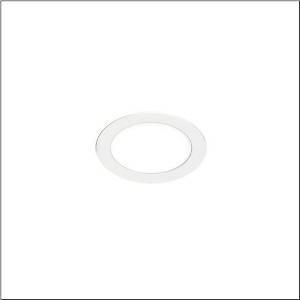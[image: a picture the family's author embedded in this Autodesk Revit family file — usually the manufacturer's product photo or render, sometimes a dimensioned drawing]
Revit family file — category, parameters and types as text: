
# Revit family: lunis_41_flat_51dr107dhba
name_source: partatom
category: Lighting Fixtures
units: mm (PartAtom-declared; Revit-internal decimal feet)

## family parameters
Cut with Voids When Loaded = No
Host = Face
Light Source = No
Part Type = Normal
Room Calculation Point = No
Round Connector Dimension = Use Diameter
Shared = No

## types (1)
- --- (1 x LED, 1360 lm, 15 W, 5700K)
    Apparent Load = 15 VA
    CIE Flux Codes = 49 80 96 100 100
    Color Rendering = 80
    Color Temperature = 5700K
    Default Elevation = 1800 mm
    Description = Lunis 41,  flat, downlight, light emission: direct distribution, LED rated luminous flux: 1.360lm, light colour: 840/857, control gear: ECG, mains connection: 230V, AC, 50/60Hz, housing, round, of aluminium, coated, traffic white (RAL 9016), diameter: 170mm, protection rating (complete): IP20, insulation class (complete): insulation class II (safety insulation), certification: CE, permissible ambient temperature for indoor applications: -20..+40°C, packaging unit: 1 piece
    Height = 0 mm  [stored 0 ft]
    Lamp = 1 x LED
    Lamp Light Flux = 1360 lm
    Lamp Power = 15 W
    Lamp count = 1
    Length = 170 mm  [stored 0.557743 ft]
    Luminous efficacy = 91 lm/W
    Manufacturer = Siteco
    ModVariant = No
    Model = 51DR107DHBA
    Mounting Place = Ceiling
    Mounting Type = Recessed
    Number of Poles = 1
    OnlyDefault = Yes
    Power Factor = 1
    Product Name = Lunis 41 flat
    Product group = downlight | ceiling recessed
    ProductGroupID = 402
    Protection Class = Protection class II
    Protection Degree = IP 20
    RLX_Detail_Level = 1
    RlxData = <blob elided: 24305 chars, md5=ac835a55>
    Socket = socket
    Standby Power = 0 W
    System Light Flux = 1360 lm
    System Power = 15 W
    Type Comments = factory setting: colour temperature 5700K
    Type Image = l_1007045.jpg
    URL = http://relux.com
    VarID = @adj_117317
    Voltage = 0 V
    Weight = 0.00 kg
    Width = 0 mm  [stored 0 ft]

note: [stored X ft] marks values corroborated as IEEE doubles in the binary element streams (Revit-internal decimal feet)

## geometry (parser evidence)
native form markers: Blend x4, Sweep x11
no freeform markers — native parametric forms only
